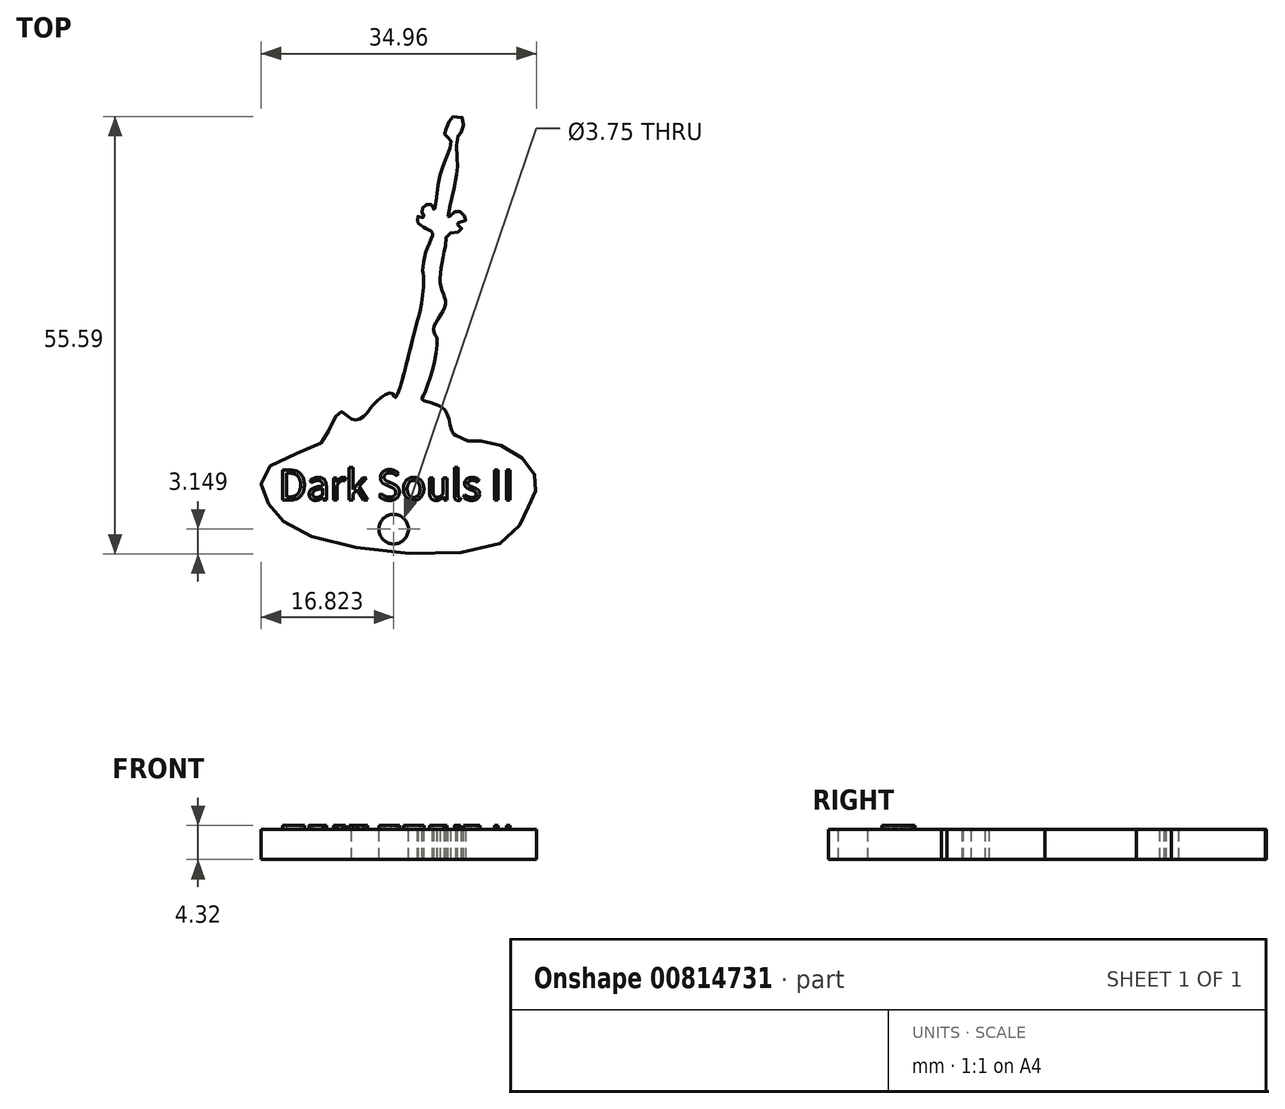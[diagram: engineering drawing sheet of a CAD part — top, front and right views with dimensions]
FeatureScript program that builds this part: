
annotation { "Feature Type Name" : "Feature", "Feature Type Description" : "" }
export const myFeature = defineFeature(function(context is Context, id is Id, definition is map)
    precondition{}
    {
        {
            var Q0;
            Q0=qCreatedBy(makeId("Top.planeOp"),FACE);
            var sketch = newSketch(context, id + "F0", { "sketchPlane" : qUnion([Q0])});
            skFitSpline(sketch, "E0", {"points": [v(5.83, 40.48) * mm, v(6.52, 40.35) * mm, v(6.4, 38.53) * mm, v(5.96, 38.1) * mm, v(5.83, 34.9) * mm, v(5.7, 32.77) * mm, v(4.7, 27.64) * mm, v(5.14, 28.14) * mm, v(6.02, 28.52) * mm, v(6.77, 27.9) * mm, v(6.9, 27.33) * mm, v(5.7, 26.95) * mm, v(6.33, 26.51) * mm, v(6.2, 25.95) * mm, v(4.7, 25.64) * mm, v(4.33, 24.07) * mm], "startDerivative": vector(16.97, 3.06) * mm, "endDerivative": vector(0.33, -26.84) * mm});
            skFitSpline(sketch, "E1", {"points": [v(4.33, 24.07) * mm, v(3.76, 18.88) * mm, v(4.33, 16.5) * mm, v(2.83, 13.55) * mm, v(3.8, 11.87) * mm, v(4.87, 8.95) * mm, v(4.33, 4.83) * mm, v(5.58, 4.12) * mm, v(6.24, 2.26) * mm, v(5.7, 0) * mm], "startDerivative": vector(-8.46, -37.88) * mm, "endDerivative": vector(-7.62, -21.7) * mm});
            skFitSpline(sketch, "E2", {"points": [v(5.7, 0) * mm, v(7.35, -0.75) * mm, v(9.34, -0.75) * mm, v(14.39, -3.1) * mm, v(15.9, -6.37) * mm, v(14.83, -9.16) * mm, v(11.24, -13.72) * mm, v(-12.49, -12.88) * mm, v(-18.37, -8.27) * mm, v(-18.46, -4.33) * mm, v(-11.38, -0.88) * mm, v(-10.4, 0.98) * mm, v(-9.2, 3.02) * mm, v(-8.9, 3.1) * mm, v(-7.62, 2.13) * mm, v(-7.09, 2.7) * mm], "startDerivative": vector(35.84, -21.67) * mm, "endDerivative": vector(13.56, 30.3) * mm});
            skFitSpline(sketch, "E3", {"points": [v(-7.09, 2.7) * mm, v(-6.5, 5.27) * mm, v(-5.36, 6.6) * mm, v(-4.52, 9.88) * mm, v(-4.3, 13.95) * mm, v(-2.57, 18.95) * mm, v(-2.35, 19.04) * mm, v(-2.84, 13.42) * mm, v(-2, 10.98) * mm, v(-1.64, 15.59) * mm, v(-1.06, 19.08) * mm, v(-0.53, 14.13) * mm, v(0, 19.93) * mm, v(0.66, 14.8) * mm, v(1.6, 19.62) * mm, v(1.46, 21.08) * mm, v(2.12, 24.07) * mm, v(2.7, 25.73) * mm, v(2, 26.26) * mm, v(0.84, 26.96) * mm], "startDerivative": vector(6.23, 59.72) * mm, "endDerivative": vector(-32.6, 21.7) * mm});
            skFitSpline(sketch, "E4", {"points": [v(0.84, 26.96) * mm, v(0.84, 27.32) * mm, v(0.84, 27.85) * mm, v(1.55, 27.67) * mm, v(1.6, 27.94) * mm, v(1.37, 28.34) * mm, v(1.6, 29.13) * mm, v(2.52, 29.36) * mm, v(2.92, 28.65) * mm, v(3.4, 31.66) * mm, v(4.33, 35.07) * mm, v(5, 37.5) * mm, v(4.33, 38.12) * mm, v(4.33, 38.74) * mm, v(5.27, 40.48) * mm, v(5.83, 40.48) * mm], "startDerivative": vector(0.96, 7.5) * mm, "endDerivative": vector(11.29, -4.06) * mm});
            skSolve(sketch);
        }
        {
            var Q0;
            Q0 = qSketchRegion(id + "F0", true);
            extrude(context, id + "F1", {"entities" : qUnion([Q0]), "depth" : 3.8 * mm, "offsetDistance" : 25.4 * mm});
        }
        {
            var Q0;
            Q0=makeQuery(id+"F1.opExtrude","CAP_FACE",FACE,{"disambiguationData":[OSD([sQuery(id+"F0.wireOp",EDGE,"E0"),sQuery(id+"F0.wireOp",EDGE,"E1"),sQuery(id+"F0.wireOp",EDGE,"E2"),sQuery(id+"F0.wireOp",EDGE,"E3"),sQuery(id+"F0.wireOp",EDGE,"E4")])],"isStart":false});
            var sketch = newSketch(context, id + "F2", { "sketchPlane" : qUnion([Q0])});
            skCircle(sketch, "E5", {"center": v(-2.24, -11.9) * mm, "radius": 1.87 * mm});
            skSolve(sketch);
        }
        {
            var Q0;
            Q0 = qSketchRegion(id + "F2", true);
            extrude(context, id + "F3", {"entities" : qUnion([Q0]), "operationType" : NewBodyOperationType.REMOVE, "oppositeDirection" : true, "depth" : 25.4 * mm, "offsetDistance" : 25.4 * mm});
        }
        {
            var Q0;
            Q0=makeQuery(id+"F1.opExtrude","CAP_FACE",FACE,{"disambiguationData":[OSD([sQuery(id+"F0.wireOp",EDGE,"E0"),sQuery(id+"F0.wireOp",EDGE,"E1"),sQuery(id+"F0.wireOp",EDGE,"E2"),sQuery(id+"F0.wireOp",EDGE,"E3"),sQuery(id+"F0.wireOp",EDGE,"E4")])],"isStart":false});
            var sketch = newSketch(context, id + "F4", { "sketchPlane" : qUnion([Q0])});
            skText(sketch, "E6", { "text": "Dark Souls II", "fontName": "NotoSansCJKtc-Regular.otf"});
            const initialGuessF4  = {"E6": [-0.01683, -0.00818, 1, 0, 0.00372]};
            skSetInitialGuess(sketch, initialGuessF4);
            skSolve(sketch);
        }
        {
            var Q0;
            Q0 = qSketchRegion(id + "F4", true);
            extrude(context, id + "F5", {"entities" : qUnion([Q0]), "operationType" : NewBodyOperationType.ADD, "depth" : 0.5 * mm, "offsetDistance" : 25.4 * mm});
        }
        {
            var Q0;
            {var subQ0=sQuery(id+"F0.wireOp",EDGE,"E3");var subQ1=sQuery(id+"F0.wireOp",EDGE,"E2");var subQ2=sQuery(id+"F0.wireOp",EDGE,"E1");var subQ3=sQuery(id+"F0.wireOp",EDGE,"E4");var subQ4=sQuery(id+"F0.wireOp",EDGE,"E0");Q0=makeQuery(id+"F5.boolean.opBoolean","SPLIT",FACE,{"disambiguationData":[TD([makeQuery(id+"F1.opExtrude","SWEPT_FACE",FACE,{"disambiguationData":[OSD([subQ4])]})])],"derivedFrom":makeQuery(id+"F1.opExtrude","CAP_FACE",FACE,{"disambiguationData":[OSD([subQ4,subQ2,subQ1,subQ0,subQ3])],"isStart":false})});}
            var sketch = newSketch(context, id + "F6", { "sketchPlane" : qUnion([Q0])});
            skFitSpline(sketch, "E7", {"points": [v(-7.56, 2.13) * mm, v(-5.74, 2.7) * mm, v(-4.74, 4) * mm, v(-2.43, 5.38) * mm, v(-1.99, 4.87) * mm, v(0.92, 15.07) * mm, v(0.99, 15.28) * mm, v(-0.55, 21.15) * mm, v(-4, 21.03) * mm, v(-8.44, 14.08) * mm, v(-7.56, 2.13) * mm]});
            skFitSpline(sketch, "E8", {"points": [v(3.34, 14.68) * mm, v(3.29, 12.45) * mm, v(1.58, 5.13) * mm, v(1.4, 4.56) * mm, v(2.83, 4.06) * mm, v(4.59, 2.7) * mm, v(5.7, 0) * mm, v(9.9, 9.76) * mm, v(3.34, 14.68) * mm]});
            skSolve(sketch);
        }
        {
            var Q0;
            {var subQ0=sQuery(id+"F6.wireOp",EDGE,"E7");var subQ1=makeQuery(id+"F1.opExtrude","CAP_EDGE",EDGE,{"disambiguationData":[OSD([sQuery(id+"F0.wireOp",EDGE,"E3")])],"isStart":false});var subQ2=makeQuery(id+"F6.imprint","INTERSECT",VERTEX,{"disambiguationData":[OD(0.0)],"derivedFrom":[subQ1,subQ0]});Q0=makeQuery(id+"F6.imprint","IMPRINT",FACE,{"disambiguationData":[TD([[makeQuery(id+"F6.imprint","IMPRINT",EDGE,{"disambiguationData":[TD([[subQ2,1.0]])],"derivedFrom":subQ0}),1.0]])]});}
            var Q1;
            {var subQ0=sQuery(id+"F6.wireOp",EDGE,"E8");var subQ1=makeQuery(id+"F1.opExtrude","CAP_EDGE",EDGE,{"disambiguationData":[OSD([sQuery(id+"F0.wireOp",EDGE,"E1")])],"isStart":false});var subQ3=makeQuery(id+"F6.imprint","INTERSECT",VERTEX,{"disambiguationData":[OD(2.0)],"derivedFrom":[subQ1,subQ0]});Q1=makeQuery(id+"F6.imprint","IMPRINT",FACE,{"disambiguationData":[TD([[makeQuery(id+"F6.imprint","IMPRINT",EDGE,{"disambiguationData":[TD([[subQ3,-1.0]])],"derivedFrom":subQ0}),1.0]])]});}
            extrude(context, id + "F7", {"entities" : qUnion([Q0, Q1]), "operationType" : NewBodyOperationType.REMOVE, "oppositeDirection" : true, "depth" : 8.23 * mm, "offsetDistance" : 25.4 * mm});
        }
        {
            var Q0;
            {var subQ0=sQuery(id+"F0.wireOp",EDGE,"E3");var subQ1=sQuery(id+"F0.wireOp",EDGE,"E2");var subQ2=sQuery(id+"F0.wireOp",EDGE,"E1");var subQ3=sQuery(id+"F0.wireOp",EDGE,"E4");var subQ4=sQuery(id+"F0.wireOp",EDGE,"E0");Q0=makeQuery(id+"F5.boolean.opBoolean","SPLIT",FACE,{"disambiguationData":[TD([makeQuery(id+"F1.opExtrude","SWEPT_FACE",FACE,{"disambiguationData":[OSD([subQ4])]})])],"derivedFrom":makeQuery(id+"F1.opExtrude","CAP_FACE",FACE,{"disambiguationData":[OSD([subQ4,subQ2,subQ1,subQ0,subQ3])],"isStart":false})});}
            var sketch = newSketch(context, id + "F8", { "sketchPlane" : qUnion([Q0])});
            skFitSpline(sketch, "E9", {"points": [v(2.96, 12.92) * mm, v(1.15, 5.32) * mm, v(0.98, 4.96) * mm, v(1.37, 4.6) * mm, v(4.17, 12.31) * mm, v(3.72, 13.15) * mm, v(3.29, 13.46) * mm, v(2.83, 13.56) * mm, v(2.96, 12.92) * mm]});
            skSolve(sketch);
        }
        {
            var Q0;
            {var subQ0=sQuery(id+"F8.wireOp",EDGE,"E9");var subQ1=makeQuery(id+"F7.boolean.opBoolean","COPY",EDGE,{"derivedFrom":makeQuery(id+"F7.opExtrude","CAP_EDGE",EDGE,{"disambiguationData":[OSD([sQuery(id+"F6.wireOp",EDGE,"E8")])],"isStart":true})});var subQ2=makeQuery(id+"F8.imprint","INTERSECT",VERTEX,{"derivedFrom":[subQ1,subQ0]});Q0=makeQuery(id+"F8.imprint","IMPRINT",FACE,{"disambiguationData":[TD([[makeQuery(id+"F8.imprint","IMPRINT",EDGE,{"disambiguationData":[TD([[subQ2,1.0]])],"derivedFrom":subQ0}),1.0]])]});}
            extrude(context, id + "F9", {"entities" : qUnion([Q0]), "operationType" : NewBodyOperationType.REMOVE, "oppositeDirection" : true, "depth" : 25.4 * mm, "offsetDistance" : 25.4 * mm});
        }
    });
